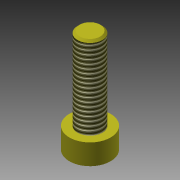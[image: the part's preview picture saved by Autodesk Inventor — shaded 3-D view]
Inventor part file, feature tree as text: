
AUTODESK INVENTOR PART (.ipt)
format: ipt  version: 2015 (Build 190159000, 159)  size: 104,960 bytes
history: native  units: mm
features: extrude x3, sketch x3, thread x1, chamfer x1
ambient origin geometry x8: Origin, YZ Plane, XZ Plane, XY Plane, X Axis, Y Axis, Z Axis, Center Point
bodies: 实体1 (feature_tree)
feature tree (8):
  extrude  "拉伸1"  Depth=2.5mm TaperAngle=0.0deg
  extrude  "拉伸2"  Depth=10.0mm TaperAngle=0.0deg
  thread  "螺纹1"  [1 undecoded]
  chamfer  "倒角1"  Distance=0.25mm Angle=45.0deg
  extrude  "拉伸3"  Depth=1.5mm
  sketch  "草图1"  dims[d0=5.0mm d1=2.5mm d2=0.0mm]
  sketch  "草图2"  dims[d3=3.0mm d4=10.0mm d5=0.0mm d6=10.0mm d7=0.0mm d8=0.25mm d9=2.0mm d10=45.0deg]
  sketch  "草图3"  dims[d11=0.2895mm d12=1.5mm d13=1.25mm d14=0.0mm]
note: 1 required parameter value undecoded (feature->parameter linkage not recoverable at this tier; creation-order binding heuristic only, values carry confidence <= 0.55)
